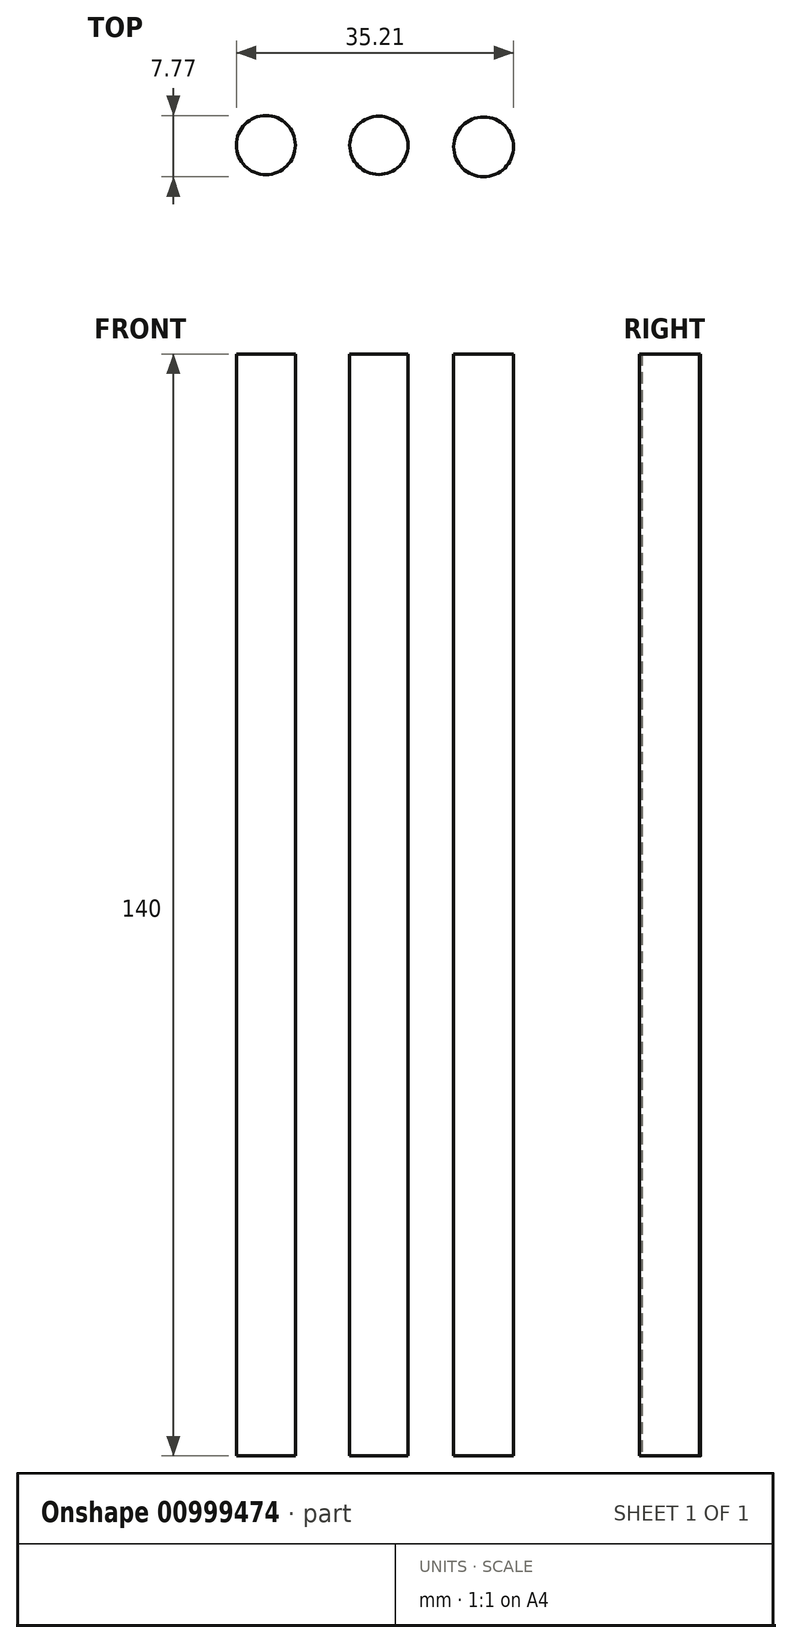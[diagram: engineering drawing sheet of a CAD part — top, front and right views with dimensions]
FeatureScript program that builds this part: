
annotation { "Feature Type Name" : "Feature", "Feature Type Description" : "" }
export const myFeature = defineFeature(function(context is Context, id is Id, definition is map)
    precondition{}
    {
        {
            var Q0;
            Q0=qCreatedBy(makeId("Top.planeOp"),FACE);
            var sketch = newSketch(context, id + "F0", { "sketchPlane" : qUnion([Q0])});
            skCircle(sketch, "E0", {"center": v(-23.22, 14.3) * mm, "radius": 3.75 * mm});
            skCircle(sketch, "E1", {"center": v(-8.87, 14.28) * mm, "radius": 3.7 * mm});
            skCircle(sketch, "E2", {"center": v(4.44, 14.09) * mm, "radius": 3.8 * mm});
            skSolve(sketch);
        }
        {
            var Q0;
            Q0=makeQuery(id+"F0.imprint","IMPRINT",FACE,{"disambiguationData":[TD([[makeQuery(id+"F0.imprint","IMPRINT",EDGE,{"derivedFrom":sQuery(id+"F0.wireOp",EDGE,"E0")}),1.0]])]});
            var Q1;
            Q1=makeQuery(id+"F0.imprint","IMPRINT",FACE,{"disambiguationData":[TD([[makeQuery(id+"F0.imprint","IMPRINT",EDGE,{"derivedFrom":sQuery(id+"F0.wireOp",EDGE,"E1")}),1.0]])]});
            var Q2;
            Q2=makeQuery(id+"F0.imprint","IMPRINT",FACE,{"disambiguationData":[TD([[makeQuery(id+"F0.imprint","IMPRINT",EDGE,{"derivedFrom":sQuery(id+"F0.wireOp",EDGE,"E2")}),1.0]])]});
            extrude(context, id + "F1", {"entities" : qUnion([Q0, Q1, Q2]), "depth" : 140 * mm, "offsetDistance" : 25 * mm});
        }
    });
